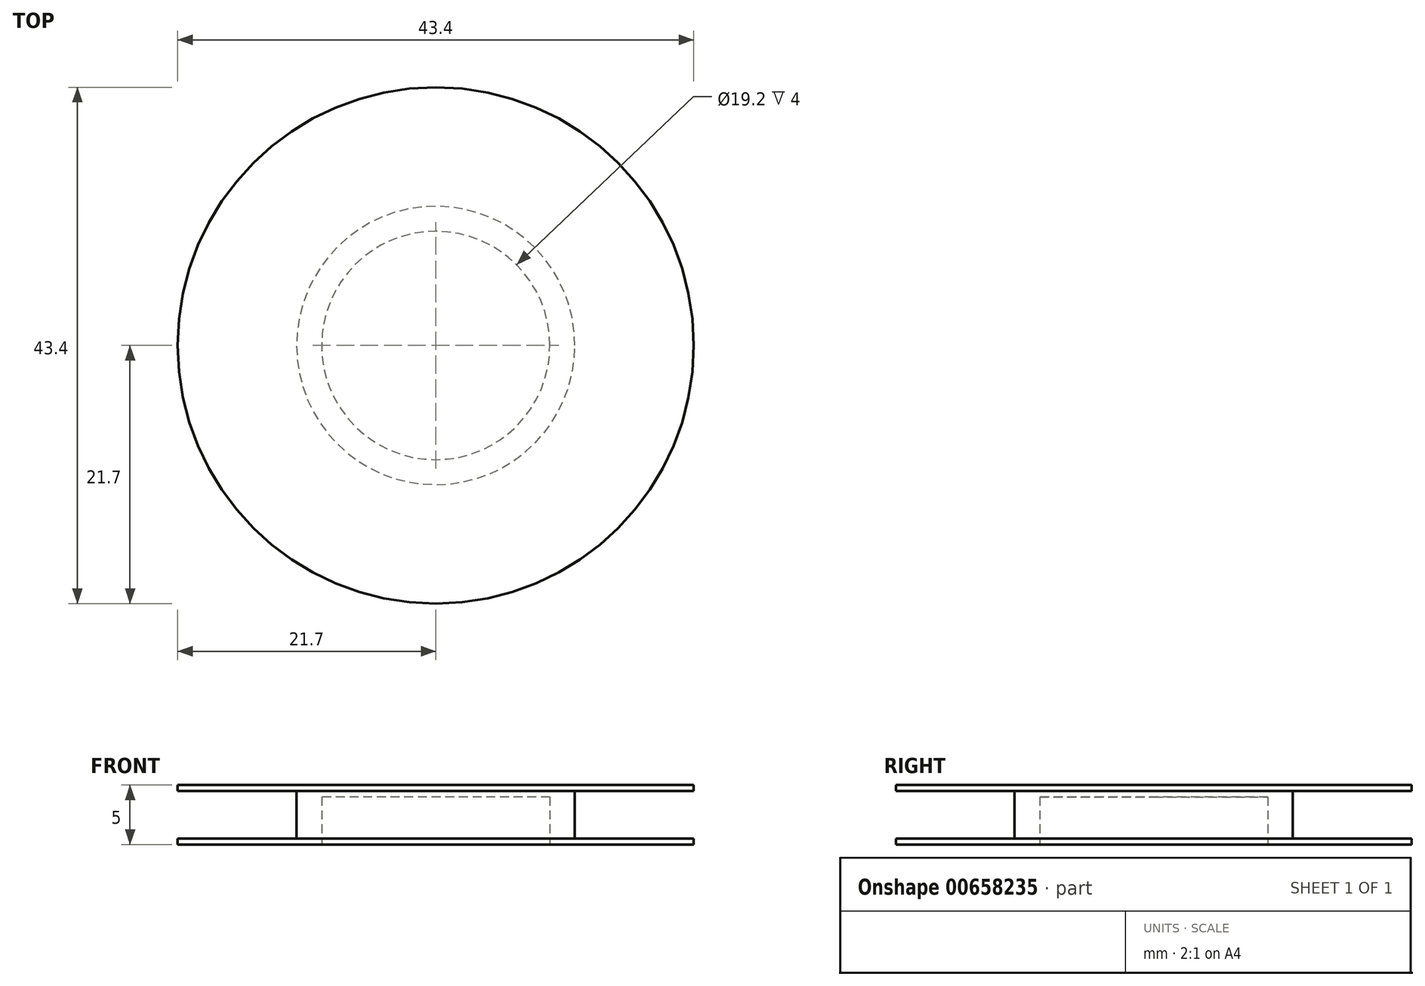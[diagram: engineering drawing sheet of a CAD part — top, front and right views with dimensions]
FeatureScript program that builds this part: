
annotation { "Feature Type Name" : "Feature", "Feature Type Description" : "" }
export const myFeature = defineFeature(function(context is Context, id is Id, definition is map)
    precondition{}
    {
        {
            var Q0;
            Q0=qCreatedBy(makeId("Top.planeOp"),FACE);
            var sketch = newSketch(context, id + "F0", { "sketchPlane" : qUnion([Q0])});
            skCircle(sketch, "E0", {"center": v(0, 0) * mm, "radius": 9.6 * mm});
            skCircle(sketch, "E1", {"center": v(0, 0) * mm, "radius": 11.7 * mm});
            skCircle(sketch, "E2", {"center": v(0, 0) * mm, "radius": 21.7 * mm});
            skSolve(sketch);
        }
        {
            var Q0;
            Q0=makeQuery(id+"F0.imprint","IMPRINT",FACE,{"disambiguationData":[TD([[makeQuery(id+"F0.imprint","IMPRINT",EDGE,{"derivedFrom":sQuery(id+"F0.wireOp",EDGE,"E0")}),-1.0]])]});
            extrude(context, id + "F1", {"entities" : qUnion([Q0]), "depth" : 5 * mm, "offsetDistance" : 25 * mm});
        }
        {
            var Q0;
            Q0=makeQuery(id+"F0.imprint","IMPRINT",FACE,{"disambiguationData":[TD([[makeQuery(id+"F0.imprint","IMPRINT",EDGE,{"derivedFrom":sQuery(id+"F0.wireOp",EDGE,"E1")}),-1.0]])]});
            extrude(context, id + "F2", {"entities" : qUnion([Q0]), "operationType" : NewBodyOperationType.ADD, "depth" : 0.5 * mm, "offsetDistance" : 25 * mm});
        }
        {
            var Q0;
            Q0=makeQuery(id+"F0.imprint","IMPRINT",FACE,{"disambiguationData":[TD([[makeQuery(id+"F0.imprint","IMPRINT",EDGE,{"derivedFrom":sQuery(id+"F0.wireOp",EDGE,"E1")}),-1.0]])]});
            extrude(context, id + "F3", {"entities" : qUnion([Q0]), "operationType" : NewBodyOperationType.ADD, "depth" : 5 * mm, "offsetDistance" : 25 * mm, "hasSecondDirection" : true, "secondDirectionOppositeDirection" : false, "secondDirectionDepth" : 4.5 * mm});
        }
        {
            var Q0;
            Q0=makeQuery(id+"F0.imprint","IMPRINT",FACE,{"disambiguationData":[TD([[makeQuery(id+"F0.imprint","IMPRINT",EDGE,{"derivedFrom":sQuery(id+"F0.wireOp",EDGE,"E0")}),1.0]])]});
            extrude(context, id + "F4", {"entities" : qUnion([Q0]), "operationType" : NewBodyOperationType.ADD, "depth" : 5 * mm, "offsetDistance" : 25 * mm, "hasSecondDirection" : true, "secondDirectionOppositeDirection" : false, "secondDirectionDepth" : 4 * mm});
        }
    });
